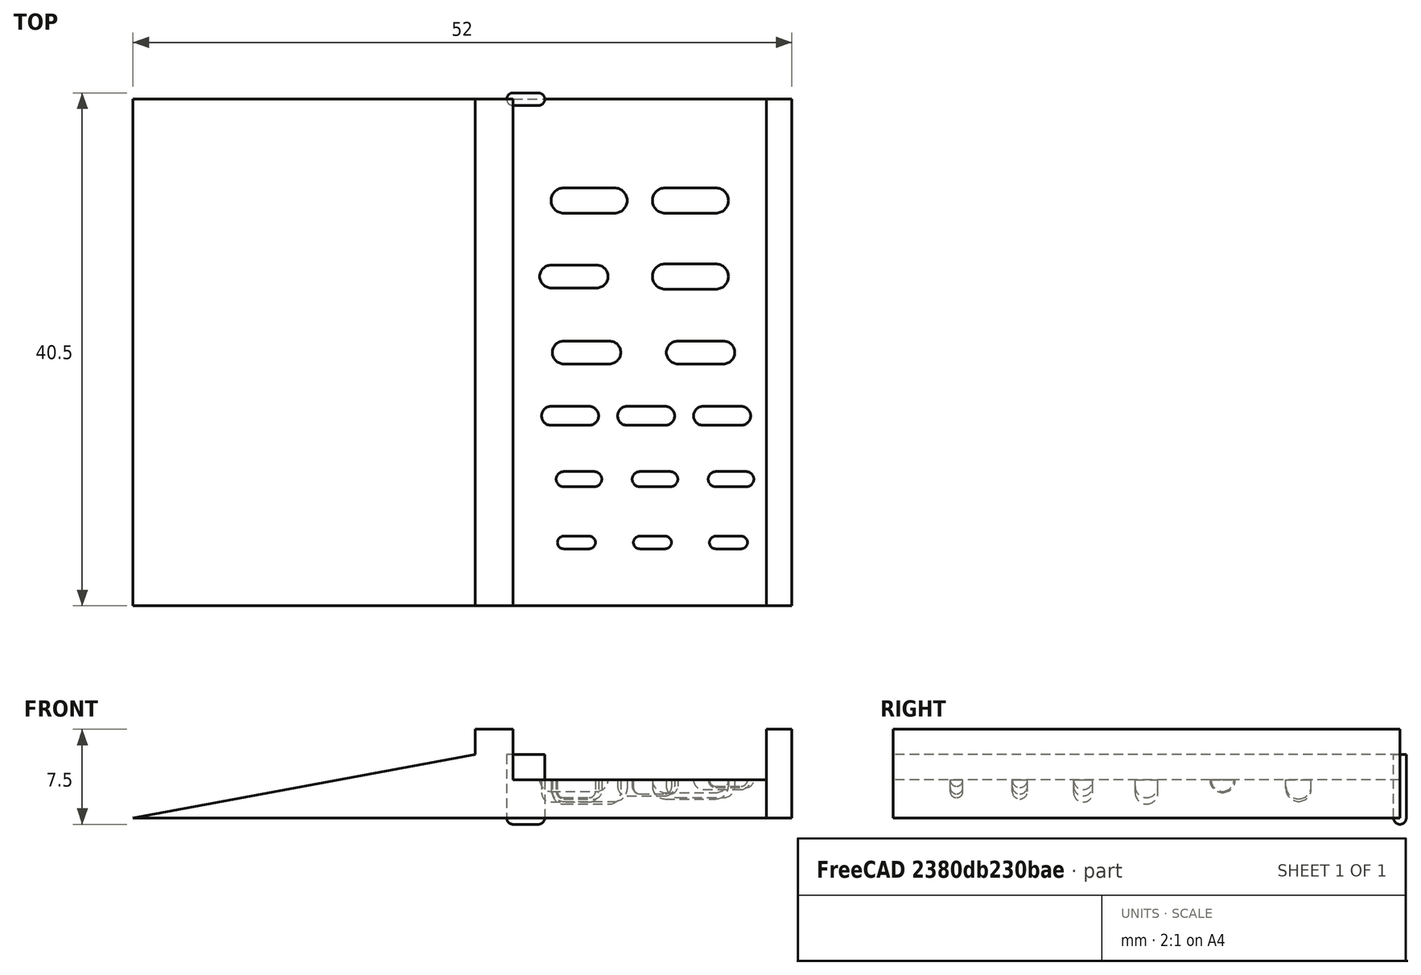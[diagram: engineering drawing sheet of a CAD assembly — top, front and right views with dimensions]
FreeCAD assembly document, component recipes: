
FREECAD ASSEMBLY — COMPONENT RECIPES ("Sarcophagus_platform_15")

This assembly document has 2 components, labeled P0..P1 below (a component is one placed body or linked part). 1 of them carries a construction recipe — the FreeCAD feature program that regenerates the part from scratch, quoted from this document or its linked companion documents; the rest are supplied as boundary geometry only. No exploded tour is included for this assembly.
COMPONENT P0 — geometry summary ("Model"; no construction recipe available for this part):
  bounding box: 20.0 x 20.0 x 20.0 mm
  tessellated surface: 180 triangles
  volume: 64 mm^3 (1% of its bounding box)
COMPONENT P1 — recipe-attached ("Tether_Platform", modeled in this document).
Construction recipe (the document's own serialized feature program — sketch geometry with constraints, then the solid features built on it; lengths are millimeters unless a unit is written):

FEATURE [Sketcher::SketchObject] Sketch
  FullyConstrained = true
  MapMode = 5
  Placement = pos=(0,0,0) rot=(1,0,0;1.5708rad)
  Support = -> [XZ_Plane]
  sketch-geometry (7):
    g0: LineSegment StartX=20 StartY=0 StartZ=0 EndX=-30 EndY=0 EndZ=0
    g1: LineSegment StartX=-30 StartY=0 StartZ=0 EndX=-3 EndY=5 EndZ=0
    g2: LineSegment StartX=-3 StartY=5 StartZ=0 EndX=-3 EndY=7 EndZ=0
    g3: LineSegment StartX=-3 StartY=7 StartZ=0 EndX=0 EndY=7 EndZ=0
    g4: LineSegment StartX=0 StartY=7 StartZ=0 EndX=0 EndY=3 EndZ=0
    g5: LineSegment StartX=0 StartY=3 StartZ=0 EndX=20 EndY=3 EndZ=0
    g6: LineSegment StartX=20 StartY=3 StartZ=0 EndX=20 EndY=0 EndZ=0
  constraints (21):
    c: PointOnObject(g0,g-1)
    c: Horizontal(g0)
    c: Coincident(g0,g1)
    c: Coincident(g1,g2)
    c: Vertical(g2)
    c: Coincident(g2,g3)
    c: PointOnObject(g3,g-2)
    c: Horizontal(g3)
    c: Coincident(g3,g4)
    c: Vertical(g4)
    c: Coincident(g4,g5)
    c: Horizontal(g5)
    c: Coincident(g5,g6)
    c: Coincident(g6,g0)
    c: Vertical(g6)
    c: Distance(g5) = 20
    c: Distance(g3) = 3
    c: Distance(g4) = 4
    c: Distance(g6) = 3
    c: Distance(g2) = 2
    c: Distance(g0) = 50
FEATURE [PartDesign::Pad] Pad
  Direction = (1,1,1)
  Length = 40
  Length2 = 100
  Placement = pos=(0,0,0) rot=(1,0,0;1.5708rad)
  Profile = -> Sketch
  Type = 0
FEATURE [PartDesign::Body] Body
  Group = -> [Sketch,Pad]
  Origin = -> Origin
  Tip = -> Pad
FEATURE [Sketcher::SketchObject] Sketch002
  FullyConstrained = true
  MapMode = 5
  Support = -> [XY_Plane001]
  sketch-geometry (4):
    g0: ArcOfCircle CenterX=0 CenterY=0 CenterZ=0 NormalX=0 NormalY=0 NormalZ=1 AngleXU=0 Radius=0.5 StartAngle=1.5708 EndAngle=4.71239
    g1: ArcOfCircle CenterX=2 CenterY=0 CenterZ=0 NormalX=0 NormalY=0 NormalZ=1 AngleXU=0 Radius=0.5 StartAngle=4.71239 EndAngle=7.85398
    g2: LineSegment StartX=-1e-16 StartY=-0.5 StartZ=0 EndX=2 EndY=-0.5 EndZ=0
    g3: LineSegment StartX=-1e-16 StartY=0.5 StartZ=0 EndX=2 EndY=0.5 EndZ=0
  constraints (9):
    c: Tangent(g0,g3) = 1.5708
    c: Tangent(g0,g2) = -1.5708
    c: Tangent(g2,g1) = -1.5708
    c: Tangent(g3,g1) = 1.5708
    c: Horizontal(g2)
    c: Equal(g0,g1)
    c: Coincident(g0,g-1)
    c: Radius(g0) = 0.5
    c: Distance(g3) = 2
FEATURE [PartDesign::FeatureBase] BaseFeature
  BaseFeature = -> Fusion
FEATURE [PartDesign::Pad] Pad001
  BaseFeature = -> BaseFeature
  Direction = (1,1,1)
  Length = 5
  Length2 = 100
  Profile = -> Sketch002
  Type = 0
FEATURE [PartDesign::ShapeBinder] CopyCut
  TraceSupport = false
FEATURE [PartDesign::Body] Body001
  BaseFeature = -> Fusion
  Group = -> [BaseFeature,Sketch002,Pad001,CopyCut]
  Origin = -> Origin001
  Tip = -> Pad001
FEATURE [PartDesign::ShapeBinder] CopyCopyCut
  TraceSupport = false
FEATURE [Sketcher::SketchObject] Sketch003
  FullyConstrained = true
  MapMode = 5
  Placement = pos=(20,0,0) rot=(0.57735,0.57735,0.57735;2.0944rad)
  Support = -> [CopyCopyCut]
  sketch-geometry (4):
    g0: LineSegment StartX=0 StartY=0 StartZ=0 EndX=-40 EndY=0 EndZ=0
    g1: LineSegment StartX=-40 StartY=0 StartZ=0 EndX=-40 EndY=7 EndZ=0
    g2: LineSegment StartX=-40 StartY=7 StartZ=0 EndX=0 EndY=7 EndZ=0
    g3: LineSegment StartX=0 StartY=7 StartZ=0 EndX=0 EndY=0 EndZ=0
  constraints (11):
    c: Coincident(g0,g1)
    c: Coincident(g1,g2)
    c: Coincident(g2,g3)
    c: Coincident(g3,g0)
    c: Horizontal(g0)
    c: Horizontal(g2)
    c: Vertical(g1)
    c: Vertical(g3)
    c: Coincident(g0,g-1)
    c: Distance(g0) = 40
    c: Distance(g1) = 7
FEATURE [PartDesign::Pad] Pad002
  Direction = (1,1,1)
  Length = 2
  Length2 = 100
  Profile = -> Sketch003
  Type = 0
FEATURE [PartDesign::Body] Body001004
  Group = -> [CopyCopyCut,Sketch003,Pad002]
  Origin = -> Origin002
  Tip = -> Pad002
PROVENANCE & LICENSES
A FreeCAD (.FCStd) document from a public repository crawl; recipes are the document's own serialized feature recipes (and, for linked parts, companion documents' recipes).
License: cern-ohl.
